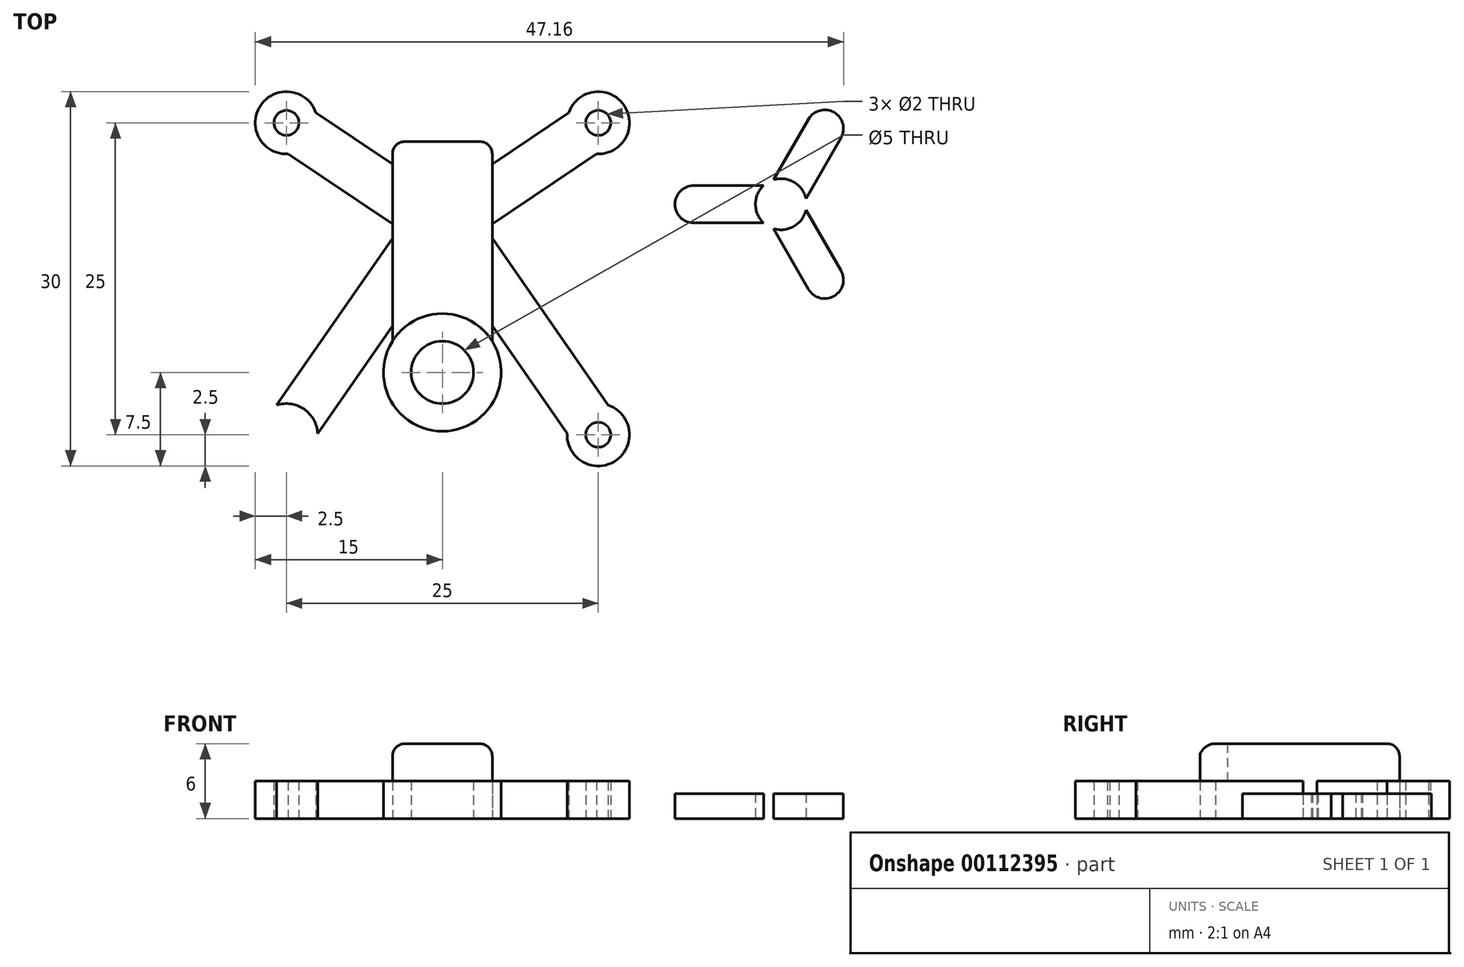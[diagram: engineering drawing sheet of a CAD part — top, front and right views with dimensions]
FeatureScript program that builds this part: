
annotation { "Feature Type Name" : "Feature", "Feature Type Description" : "" }
export const myFeature = defineFeature(function(context is Context, id is Id, definition is map)
    precondition{}
    {
        {
            var Q0;
            Q0=qCreatedBy(makeId("Top.planeOp"),FACE);
            var sketch = newSketch(context, id + "F0", { "sketchPlane" : qUnion([Q0])});
            skCircle(sketch, "E0", {"center": v(-12.5, 12.5) * mm, "radius": 1 * mm});
            skLineSegment(sketch, "E1.bottom", {"start": v(-4, 11) * mm, "end": v(4, 11) * mm});
            skLineSegment(sketch, "E1.top", {"start": v(-4, -5) * mm, "end": v(4, -5) * mm});
            skLineSegment(sketch, "E1.left", {"start": v(-4, 11) * mm, "end": v(-4, -5) * mm});
            skLineSegment(sketch, "E1.right", {"start": v(4, 11) * mm, "end": v(4, -5) * mm});
            skPoint(sketch, "E1.middle", {"position": v(0, 3) * mm});
            skLineSegment(sketch, "E2", {"start": v(-11.94, 13.33) * mm, "end": v(-4, 8) * mm});
            skLineSegment(sketch, "E3", {"start": v(-13.06, 11.67) * mm, "end": v(-4, 5.6) * mm});
            skCircle(sketch, "E4.0", {"center": v(-12.5, 12.5) * mm, "radius": 2.5 * mm});
            skLineSegment(sketch, "E5", {"start": v(-10.14, 13.32) * mm, "end": v(-4, 9.2) * mm});
            skLineSegment(sketch, "E6", {"start": v(-12.37, 10) * mm, "end": v(-4, 4.39) * mm});
            skLineSegment(sketch, "E7.MirrorCS", {"start": v(13.06, 11.67) * mm, "end": v(4, 5.6) * mm});
            skLineSegment(sketch, "E8.MirrorCS", {"start": v(11.94, 13.33) * mm, "end": v(4, 8) * mm});
            skLineSegment(sketch, "E9.MirrorCS", {"start": v(10.14, 13.32) * mm, "end": v(4, 9.2) * mm});
            skLineSegment(sketch, "E10.MirrorCS", {"start": v(12.37, 10) * mm, "end": v(4, 4.39) * mm});
            skCircle(sketch, "E11.MirrorC", {"center": v(12.5, 12.5) * mm, "radius": 1 * mm});
            skCircle(sketch, "E12.MirrorC", {"center": v(12.5, 12.5) * mm, "radius": 2.5 * mm});
            skCircle(sketch, "E13.MirrorC", {"center": v(-12.5, -12.5) * mm, "radius": 2.5 * mm});
            skCircle(sketch, "E14.MirrorC", {"center": v(-12.5, -12.5) * mm, "radius": 1 * mm});
            skLineSegment(sketch, "E15", {"start": v(-11.68, -13.07) * mm, "end": v(-4, -2) * mm});
            skLineSegment(sketch, "E16", {"start": v(-13.32, -11.93) * mm, "end": v(-4, 1.5) * mm});
            skLineSegment(sketch, "E17", {"start": v(-10, -12.4) * mm, "end": v(-4, -3.75) * mm});
            skLineSegment(sketch, "E18", {"start": v(-13.29, -10.13) * mm, "end": v(-4, 3.26) * mm});
            skLineSegment(sketch, "E19.MirrorCS", {"start": v(10, -12.4) * mm, "end": v(4, -3.75) * mm});
            skCircle(sketch, "E20.MirrorC", {"center": v(12.5, -12.5) * mm, "radius": 1 * mm});
            skLineSegment(sketch, "E21.MirrorCS", {"start": v(13.29, -10.13) * mm, "end": v(4, 3.26) * mm});
            skLineSegment(sketch, "E22.MirrorCS", {"start": v(11.68, -13.07) * mm, "end": v(4, -2) * mm});
            skLineSegment(sketch, "E23.MirrorCS", {"start": v(13.32, -11.93) * mm, "end": v(4, 1.5) * mm});
            skCircle(sketch, "E24.MirrorC", {"center": v(12.5, -12.5) * mm, "radius": 2.5 * mm});
            skLineSegment(sketch, "E25", {"start": v(4, 11) * mm, "end": v(4, 19.12) * mm, "construction": true});
            skCircle(sketch, "E26", {"center": v(27.16, 5.98) * mm, "radius": 1.05 * mm});
            skCircle(sketch, "E27", {"center": v(27.16, 5.98) * mm, "radius": 2.05 * mm});
            skCircle(sketch, "E28", {"center": v(20.16, 5.98) * mm, "radius": 1.5 * mm});
            skLineSegment(sketch, "E29", {"start": v(20.16, 7.48) * mm, "end": v(25.76, 7.48) * mm});
            skLineSegment(sketch, "E30", {"start": v(20.16, 4.48) * mm, "end": v(25.76, 4.48) * mm});
            skCircle(sketch, "E31.1.0", {"center": v(30.66, -0.08) * mm, "radius": 1.5 * mm});
            skLineSegment(sketch, "E31.1.1", {"start": v(31.95, 0.67) * mm, "end": v(29.15, 5.52) * mm});
            skLineSegment(sketch, "E31.1.2", {"start": v(29.36, -0.83) * mm, "end": v(26.55, 4.02) * mm});
            skCircle(sketch, "E31.2.0", {"center": v(30.66, 12.04) * mm, "radius": 1.5 * mm});
            skLineSegment(sketch, "E31.2.1", {"start": v(29.36, 12.79) * mm, "end": v(26.55, 7.94) * mm});
            skLineSegment(sketch, "E31.2.2", {"start": v(31.95, 11.29) * mm, "end": v(29.15, 6.44) * mm});
            skCircle(sketch, "E32", {"center": v(0, -7.5) * mm, "radius": 2.5 * mm});
            skCircle(sketch, "E33", {"center": v(0, -7.5) * mm, "radius": 4.72 * mm});
            skSolve(sketch);
        }
        {
            var Q0;
            {var subQ4=sQuery(id+"F0.wireOp",EDGE,"E0");var subQ7=sQuery(id+"F0.wireOp",EDGE,"E2");var subQ8=makeQuery(id+"F0.imprint","INTERSECT",VERTEX,{"derivedFrom":[subQ4,subQ7]});Q0=makeQuery(id+"F0.imprint","IMPRINT",FACE,{"disambiguationData":[TD([[makeQuery(id+"F0.imprint","IMPRINT",EDGE,{"disambiguationData":[TD([[subQ8,-1.0]])],"derivedFrom":subQ4}),-1.0]])]});}
            var Q1;
            {var subQ3=sQuery(id+"F0.wireOp",EDGE,"E5");Q1=makeQuery(id+"F0.imprint","IMPRINT",FACE,{"disambiguationData":[TD([[makeQuery(id+"F0.imprint","IMPRINT",EDGE,{"derivedFrom":subQ3}),-1.0]])]});}
            var Q2;
            {var subQ0=sQuery(id+"F0.wireOp",EDGE,"E2");var subQ1=sQuery(id+"F0.wireOp",EDGE,"E1.left");var subQ2=makeQuery(id+"F0.imprint","INTERSECT",VERTEX,{"derivedFrom":[subQ1,subQ0]});Q2=makeQuery(id+"F0.imprint","IMPRINT",FACE,{"disambiguationData":[TD([[makeQuery(id+"F0.imprint","IMPRINT",EDGE,{"disambiguationData":[TD([[subQ2,-1.0]])],"derivedFrom":subQ1}),-1.0]])]});}
            var Q3;
            {var subQ0=sQuery(id+"F0.wireOp",EDGE,"E2");var subQ1=sQuery(id+"F0.wireOp",EDGE,"E0");var subQ2=makeQuery(id+"F0.imprint","INTERSECT",VERTEX,{"derivedFrom":[subQ1,subQ0]});Q3=makeQuery(id+"F0.imprint","IMPRINT",FACE,{"disambiguationData":[TD([[makeQuery(id+"F0.imprint","IMPRINT",EDGE,{"disambiguationData":[TD([[subQ2,1.0]])],"derivedFrom":subQ1}),-1.0]])]});}
            var Q4;
            {var subQ3=sQuery(id+"F0.wireOp",EDGE,"E6");Q4=makeQuery(id+"F0.imprint","IMPRINT",FACE,{"disambiguationData":[TD([[makeQuery(id+"F0.imprint","IMPRINT",EDGE,{"derivedFrom":subQ3}),1.0]])]});}
            var Q5;
            {var subQ14=sQuery(id+"F0.wireOp",EDGE,"E1.bottom");Q5=makeQuery(id+"F0.imprint","IMPRINT",FACE,{"disambiguationData":[TD([[makeQuery(id+"F0.imprint","IMPRINT",EDGE,{"derivedFrom":subQ14}),-1.0]])]});}
            var Q6;
            {var subQ3=sQuery(id+"F0.wireOp",EDGE,"E9.MirrorCS");Q6=makeQuery(id+"F0.imprint","IMPRINT",FACE,{"disambiguationData":[TD([[makeQuery(id+"F0.imprint","IMPRINT",EDGE,{"derivedFrom":subQ3}),1.0]])]});}
            var Q7;
            {var subQ3=sQuery(id+"F0.wireOp",EDGE,"E11.MirrorC");var subQ7=sQuery(id+"F0.wireOp",EDGE,"E7.MirrorCS");var subQ8=makeQuery(id+"F0.imprint","INTERSECT",VERTEX,{"derivedFrom":[subQ7,subQ3]});Q7=makeQuery(id+"F0.imprint","IMPRINT",FACE,{"disambiguationData":[TD([[makeQuery(id+"F0.imprint","IMPRINT",EDGE,{"disambiguationData":[TD([[subQ8,-1.0]])],"derivedFrom":subQ7}),1.0]])]});}
            var Q8;
            {var subQ0=sQuery(id+"F0.wireOp",EDGE,"E11.MirrorC");var subQ1=sQuery(id+"F0.wireOp",EDGE,"E7.MirrorCS");var subQ2=makeQuery(id+"F0.imprint","INTERSECT",VERTEX,{"derivedFrom":[subQ1,subQ0]});Q8=makeQuery(id+"F0.imprint","IMPRINT",FACE,{"disambiguationData":[TD([[makeQuery(id+"F0.imprint","IMPRINT",EDGE,{"disambiguationData":[TD([[subQ2,-1.0]])],"derivedFrom":subQ1}),-1.0]])]});}
            var Q9;
            {var subQ0=sQuery(id+"F0.wireOp",EDGE,"E7.MirrorCS");var subQ1=sQuery(id+"F0.wireOp",EDGE,"E1.right");var subQ2=makeQuery(id+"F0.imprint","INTERSECT",VERTEX,{"derivedFrom":[subQ1,subQ0]});Q9=makeQuery(id+"F0.imprint","IMPRINT",FACE,{"disambiguationData":[TD([[makeQuery(id+"F0.imprint","IMPRINT",EDGE,{"disambiguationData":[TD([[subQ2,1.0]])],"derivedFrom":subQ1}),1.0]])]});}
            var Q10;
            {var subQ3=sQuery(id+"F0.wireOp",EDGE,"E10.MirrorCS");Q10=makeQuery(id+"F0.imprint","IMPRINT",FACE,{"disambiguationData":[TD([[makeQuery(id+"F0.imprint","IMPRINT",EDGE,{"derivedFrom":subQ3}),-1.0]])]});}
            var Q11;
            {var subQ0=sQuery(id+"F0.wireOp",EDGE,"E21.MirrorCS");Q11=makeQuery(id+"F0.imprint","IMPRINT",FACE,{"disambiguationData":[TD([[makeQuery(id+"F0.imprint","IMPRINT",EDGE,{"derivedFrom":subQ0}),1.0]])]});}
            var Q12;
            {var subQ0=sQuery(id+"F0.wireOp",EDGE,"E22.MirrorCS");var subQ1=sQuery(id+"F0.wireOp",EDGE,"E1.right");var subQ2=makeQuery(id+"F0.imprint","INTERSECT",VERTEX,{"derivedFrom":[subQ1,subQ0]});Q12=makeQuery(id+"F0.imprint","IMPRINT",FACE,{"disambiguationData":[TD([[makeQuery(id+"F0.imprint","IMPRINT",EDGE,{"disambiguationData":[TD([[subQ2,1.0]])],"derivedFrom":subQ1}),1.0]])]});}
            var Q13;
            {var subQ0=sQuery(id+"F0.wireOp",EDGE,"E19.MirrorCS");Q13=makeQuery(id+"F0.imprint","IMPRINT",FACE,{"disambiguationData":[TD([[makeQuery(id+"F0.imprint","IMPRINT",EDGE,{"derivedFrom":subQ0}),-1.0]])]});}
            var Q14;
            {var subQ3=sQuery(id+"F0.wireOp",EDGE,"E18");Q14=makeQuery(id+"F0.imprint","IMPRINT",FACE,{"disambiguationData":[TD([[makeQuery(id+"F0.imprint","IMPRINT",EDGE,{"derivedFrom":subQ3}),-1.0]])]});}
            var Q15;
            {var subQ0=sQuery(id+"F0.wireOp",EDGE,"E15");var subQ1=sQuery(id+"F0.wireOp",EDGE,"E1.left");var subQ2=makeQuery(id+"F0.imprint","INTERSECT",VERTEX,{"derivedFrom":[subQ1,subQ0]});Q15=makeQuery(id+"F0.imprint","IMPRINT",FACE,{"disambiguationData":[TD([[makeQuery(id+"F0.imprint","IMPRINT",EDGE,{"disambiguationData":[TD([[subQ2,1.0]])],"derivedFrom":subQ1}),-1.0]])]});}
            var Q16;
            {var subQ3=sQuery(id+"F0.wireOp",EDGE,"E17");Q16=makeQuery(id+"F0.imprint","IMPRINT",FACE,{"disambiguationData":[TD([[makeQuery(id+"F0.imprint","IMPRINT",EDGE,{"derivedFrom":subQ3}),1.0]])]});}
            var Q17;
            {var subQ5=sQuery(id+"F0.wireOp",EDGE,"E13.MirrorC");var subQ6=makeQuery(id+"F0.imprint","INTERSECT",VERTEX,{"derivedFrom":[subQ5,sQuery(id+"F0.wireOp",EDGE,"E18")]});Q17=makeQuery(id+"F0.imprint","IMPRINT",FACE,{"disambiguationData":[TD([[makeQuery(id+"F0.imprint","IMPRINT",EDGE,{"disambiguationData":[TD([[subQ6,-1.0]])],"derivedFrom":subQ5}),-1.0]])]});}
            var Q18;
            {var subQ0=sQuery(id+"F0.wireOp",EDGE,"E16");var subQ1=sQuery(id+"F0.wireOp",EDGE,"E13.MirrorC");var subQ2=makeQuery(id+"F0.imprint","INTERSECT",VERTEX,{"derivedFrom":[subQ1,subQ0]});Q18=makeQuery(id+"F0.imprint","IMPRINT",FACE,{"disambiguationData":[TD([[makeQuery(id+"F0.imprint","IMPRINT",EDGE,{"disambiguationData":[TD([[subQ2,-1.0]])],"derivedFrom":subQ1}),-1.0]])]});}
            var Q19;
            {var subQ4=sQuery(id+"F0.wireOp",EDGE,"E20.MirrorC");var subQ6=sQuery(id+"F0.wireOp",EDGE,"E22.MirrorCS");var subQ7=makeQuery(id+"F0.imprint","INTERSECT",VERTEX,{"derivedFrom":[subQ4,subQ6]});Q19=makeQuery(id+"F0.imprint","IMPRINT",FACE,{"disambiguationData":[TD([[makeQuery(id+"F0.imprint","IMPRINT",EDGE,{"disambiguationData":[TD([[subQ7,-1.0]])],"derivedFrom":subQ4}),-1.0]])]});}
            var Q20;
            {var subQ0=sQuery(id+"F0.wireOp",EDGE,"E22.MirrorCS");var subQ1=sQuery(id+"F0.wireOp",EDGE,"E20.MirrorC");var subQ2=makeQuery(id+"F0.imprint","INTERSECT",VERTEX,{"derivedFrom":[subQ1,subQ0]});Q20=makeQuery(id+"F0.imprint","IMPRINT",FACE,{"disambiguationData":[TD([[makeQuery(id+"F0.imprint","IMPRINT",EDGE,{"disambiguationData":[TD([[subQ2,1.0]])],"derivedFrom":subQ1}),-1.0]])]});}
            var Q21;
            {var subQ1=sQuery(id+"F0.wireOp",EDGE,"E1.top");var subQ3=makeQuery(id+"F0.imprint","INTERSECT",VERTEX,{"derivedFrom":[subQ1,sQuery(id+"F0.wireOp",EDGE,"E32")]});Q21=makeQuery(id+"F0.imprint","IMPRINT",FACE,{"disambiguationData":[TD([[makeQuery(id+"F0.imprint","IMPRINT",EDGE,{"disambiguationData":[TD([[subQ3,1.0]])],"derivedFrom":subQ1}),1.0]])]});}
            var Q22;
            {var subQ3=sQuery(id+"F0.wireOp",EDGE,"E32");Q22=makeQuery(id+"F0.imprint","IMPRINT",FACE,{"disambiguationData":[TD([[makeQuery(id+"F0.imprint","IMPRINT",EDGE,{"derivedFrom":subQ3}),-1.0]])]});}
            extrude(context, id + "F1", {"entities" : qUnion([Q0, Q1, Q2, Q3, Q4, Q5, Q6, Q7, Q8, Q9, Q10, Q11, Q12, Q13, Q14, Q15, Q16, Q17, Q18, Q19, Q20, Q21, Q22]), "depth" : 3 * mm});
        }
        {
            var Q0;
            {var subQ14=sQuery(id+"F0.wireOp",EDGE,"E1.bottom");Q0=makeQuery(id+"F0.imprint","IMPRINT",FACE,{"disambiguationData":[TD([[makeQuery(id+"F0.imprint","IMPRINT",EDGE,{"derivedFrom":subQ14}),-1.0]])]});}
            extrude(context, id + "F2", {"entities" : qUnion([Q0]), "operationType" : NewBodyOperationType.ADD, "depth" : 6 * mm});
        }
        {
            var Q0;
            {var subQ0=sQuery(id+"F0.wireOp",EDGE,"E31.1.1");Q0=makeQuery(id+"F0.imprint","IMPRINT",FACE,{"disambiguationData":[TD([[makeQuery(id+"F0.imprint","IMPRINT",EDGE,{"derivedFrom":subQ0}),1.0]])]});}
            var Q1;
            {var subQ0=sQuery(id+"F0.wireOp",EDGE,"E28");var subQ1=makeQuery(id+"F0.imprint","INTERSECT",VERTEX,{"derivedFrom":[subQ0,sQuery(id+"F0.wireOp",EDGE,"E29")]});Q1=makeQuery(id+"F0.imprint","IMPRINT",FACE,{"disambiguationData":[TD([[makeQuery(id+"F0.imprint","IMPRINT",EDGE,{"disambiguationData":[TD([[subQ1,-1.0]])],"derivedFrom":subQ0}),1.0]])]});}
            var Q2;
            {var subQ0=sQuery(id+"F0.wireOp",EDGE,"E31.1.0");var subQ1=makeQuery(id+"F0.imprint","INTERSECT",VERTEX,{"derivedFrom":[subQ0,sQuery(id+"F0.wireOp",EDGE,"E31.1.1")]});Q2=makeQuery(id+"F0.imprint","IMPRINT",FACE,{"disambiguationData":[TD([[makeQuery(id+"F0.imprint","IMPRINT",EDGE,{"disambiguationData":[TD([[subQ1,1.0]])],"derivedFrom":subQ0}),1.0]])]});}
            var Q3;
            {var subQ0=sQuery(id+"F0.wireOp",EDGE,"E31.2.0");var subQ1=makeQuery(id+"F0.imprint","INTERSECT",VERTEX,{"derivedFrom":[subQ0,sQuery(id+"F0.wireOp",EDGE,"E31.2.1")]});Q3=makeQuery(id+"F0.imprint","IMPRINT",FACE,{"disambiguationData":[TD([[makeQuery(id+"F0.imprint","IMPRINT",EDGE,{"disambiguationData":[TD([[subQ1,1.0]])],"derivedFrom":subQ0}),1.0]])]});}
            var Q4;
            {var subQ0=sQuery(id+"F0.wireOp",EDGE,"E31.2.1");Q4=makeQuery(id+"F0.imprint","IMPRINT",FACE,{"disambiguationData":[TD([[makeQuery(id+"F0.imprint","IMPRINT",EDGE,{"derivedFrom":subQ0}),1.0]])]});}
            var Q5;
            {var subQ0=sQuery(id+"F0.wireOp",EDGE,"E29");Q5=makeQuery(id+"F0.imprint","IMPRINT",FACE,{"disambiguationData":[TD([[makeQuery(id+"F0.imprint","IMPRINT",EDGE,{"derivedFrom":subQ0}),-1.0]])]});}
            var Q6;
            Q6=makeQuery(id+"F0.imprint","IMPRINT",FACE,{"disambiguationData":[TD([[makeQuery(id+"F0.imprint","IMPRINT",EDGE,{"derivedFrom":sQuery(id+"F0.wireOp",EDGE,"E26")}),-1.0]])]});
            extrude(context, id + "F3", {"entities" : qUnion([Q0, Q1, Q2, Q3, Q4, Q5, Q6]), "depth" : 2 * mm});
        }
        {
            var Q0;
            Q0=makeQuery(id+"F2.opExtrude","CAP_EDGE",EDGE,{"disambiguationData":[OSD([sQuery(id+"F0.wireOp",EDGE,"E1.left")])],"isStart":false});
            var Q1;
            Q1=makeQuery(id+"F2.opExtrude","CAP_EDGE",EDGE,{"disambiguationData":[OSD([sQuery(id+"F0.wireOp",EDGE,"E1.bottom")])],"isStart":false});
            var Q2;
            Q2=makeQuery(id+"F2.opExtrude","CAP_EDGE",EDGE,{"disambiguationData":[OSD([sQuery(id+"F0.wireOp",EDGE,"E1.right")])],"isStart":false});
            var Q3;
            {var subQ0=sQuery(id+"F0.wireOp",EDGE,"E1.right");var subQ1=sQuery(id+"F0.wireOp",EDGE,"E1.bottom");Q3=makeQuery(id+"F2.boolean.opBoolean","MERGE",EDGE,{"derivedFrom":[makeQuery(id+"F1.opExtrude","SWEPT_EDGE",EDGE,{"disambiguationData":[OSD([subQ1,subQ0])]}),makeQuery(id+"F2.opExtrude","SWEPT_EDGE",EDGE,{"disambiguationData":[OSD([subQ1,subQ0])]})]});}
            var Q4;
            {var subQ0=sQuery(id+"F0.wireOp",EDGE,"E1.left");var subQ1=sQuery(id+"F0.wireOp",EDGE,"E1.bottom");Q4=makeQuery(id+"F2.boolean.opBoolean","MERGE",EDGE,{"derivedFrom":[makeQuery(id+"F1.opExtrude","SWEPT_EDGE",EDGE,{"disambiguationData":[OSD([subQ1,subQ0])]}),makeQuery(id+"F2.opExtrude","SWEPT_EDGE",EDGE,{"disambiguationData":[OSD([subQ1,subQ0])]})]});}
            fillet(context, id + "F4", {"entities" : qUnion([Q0, Q1, Q2, Q3, Q4]), "radius" : 1 * mm, "tangentPropagation" : true, "allowEdgeOverflow" : false});
        }
    });
